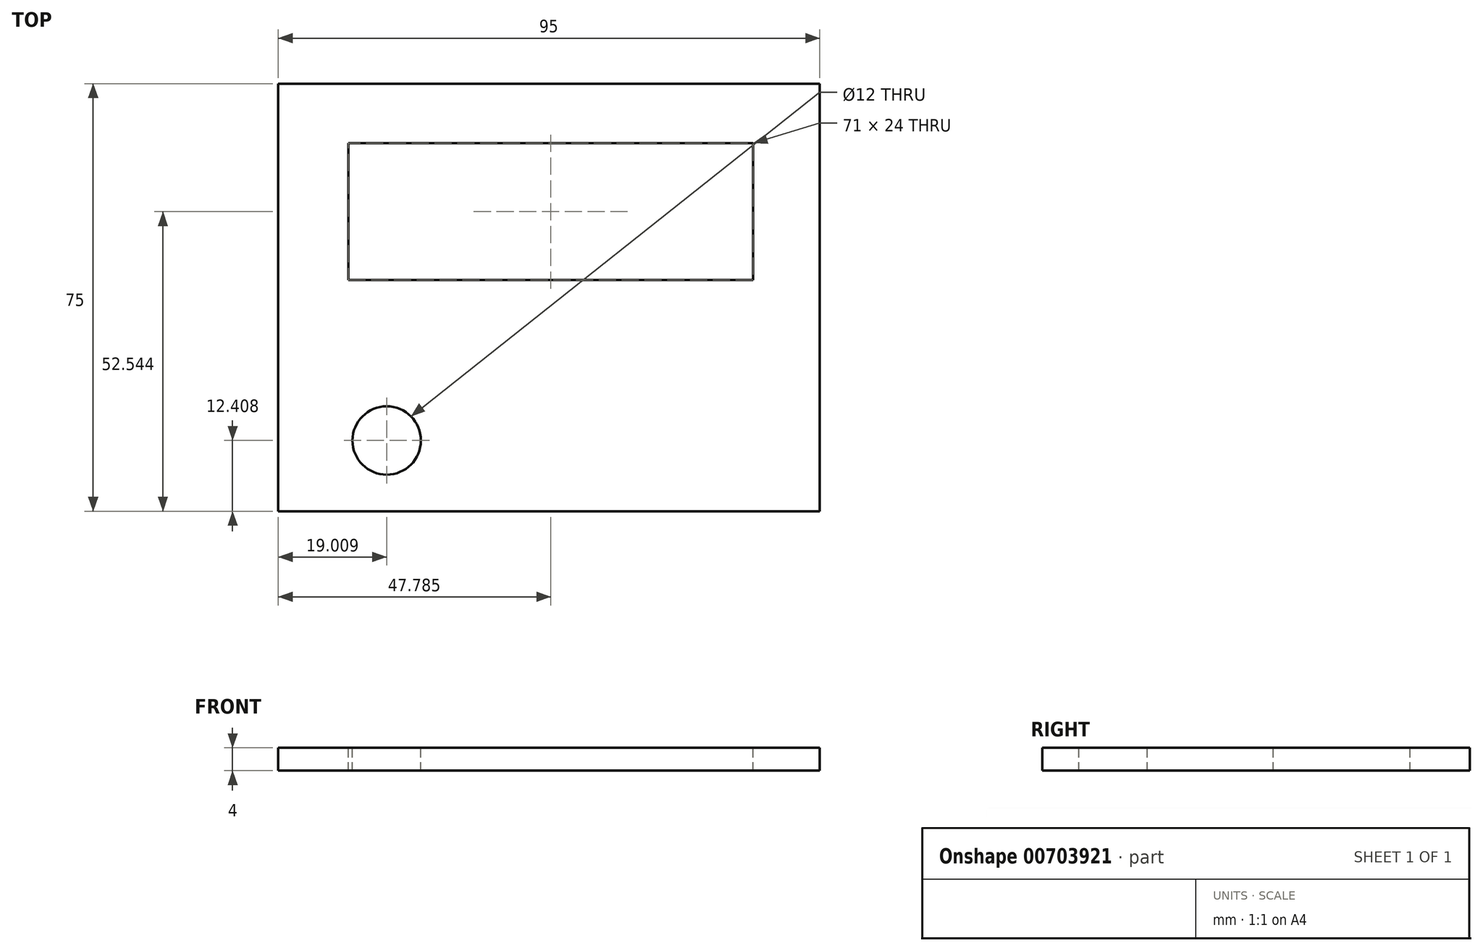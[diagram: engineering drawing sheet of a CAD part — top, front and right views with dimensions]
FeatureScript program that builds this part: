
annotation { "Feature Type Name" : "Feature", "Feature Type Description" : "" }
export const myFeature = defineFeature(function(context is Context, id is Id, definition is map)
    precondition{}
    {
        {
            var Q0;
            Q0=qCreatedBy(makeId("Top.planeOp"),FACE);
            var sketch = newSketch(context, id + "F0", { "sketchPlane" : qUnion([Q0])});
            skLineSegment(sketch, "E0.bottom", {"start": v(-67.71, 35.74) * mm, "end": v(27.29, 35.74) * mm});
            skLineSegment(sketch, "E0.top", {"start": v(-67.71, -39.26) * mm, "end": v(27.29, -39.26) * mm});
            skLineSegment(sketch, "E0.left", {"start": v(-67.71, 35.74) * mm, "end": v(-67.71, -39.26) * mm});
            skLineSegment(sketch, "E0.right", {"start": v(27.29, 35.74) * mm, "end": v(27.29, -39.26) * mm});
            skSolve(sketch);
        }
        {
            var Q0;
            Q0 = qSketchRegion(id + "F0", true);
            extrude(context, id + "F1", {"entities" : qUnion([Q0]), "depth" : 4 * mm, "offsetDistance" : 25 * mm});
        }
        {
            var Q0;
            Q0=makeQuery(id+"F1.opExtrude","CAP_FACE",FACE,{"disambiguationData":[OSD([sQuery(id+"F0.wireOp",EDGE,"E0.bottom"),sQuery(id+"F0.wireOp",EDGE,"E0.top"),sQuery(id+"F0.wireOp",EDGE,"E0.left"),sQuery(id+"F0.wireOp",EDGE,"E0.right")])],"isStart":false});
            var sketch = newSketch(context, id + "F2", { "sketchPlane" : qUnion([Q0])});
            skLineSegment(sketch, "E1.bottom", {"start": v(-55.42, 25.28) * mm, "end": v(15.58, 25.28) * mm});
            skLineSegment(sketch, "E1.top", {"start": v(-55.42, 1.28) * mm, "end": v(15.58, 1.28) * mm});
            skLineSegment(sketch, "E1.left", {"start": v(-55.42, 25.28) * mm, "end": v(-55.42, 1.28) * mm});
            skLineSegment(sketch, "E1.right", {"start": v(15.58, 25.28) * mm, "end": v(15.58, 1.28) * mm});
            skSolve(sketch);
        }
        {
            var Q0;
            Q0 = qSketchRegion(id + "F2", true);
            extrude(context, id + "F3", {"entities" : qUnion([Q0]), "operationType" : NewBodyOperationType.REMOVE, "oppositeDirection" : true, "depth" : 25 * mm, "offsetDistance" : 25 * mm});
        }
        {
            var Q0;
            Q0=makeQuery(id+"F2.imprint","IMPRINT",FACE,{"disambiguationData":[TD([[makeQuery(id+"F2.imprint","IMPRINT",EDGE,{"derivedFrom":sQuery(id+"F2.wireOp",EDGE,"E1.bottom")}),1.0]])]});
            var sketch = newSketch(context, id + "F4", { "sketchPlane" : qUnion([Q0])});
            skLineSegment(sketch, "E2.bottom", {"start": v(-24.31, -5.45) * mm, "end": v(-12.31, -5.45) * mm});
            skLineSegment(sketch, "E2.top", {"start": v(-24.31, -17.45) * mm, "end": v(-12.31, -17.45) * mm});
            skLineSegment(sketch, "E2.left", {"start": v(-24.31, -5.45) * mm, "end": v(-24.31, -17.45) * mm});
            skLineSegment(sketch, "E2.right", {"start": v(-12.31, -5.45) * mm, "end": v(-12.31, -17.45) * mm});
            skSolve(sketch);
        }
        {
            var Q0;
            Q0=makeQuery(id+"F4.imprint","IMPRINT",FACE,{"disambiguationData":[TD([[makeQuery(id+"F4.imprint","IMPRINT",EDGE,{"derivedFrom":sQuery(id+"F4.wireOp",EDGE,"E2.bottom")}),1.0]])]});
            var sketch = newSketch(context, id + "F5", { "sketchPlane" : qUnion([Q0])});
            skCircle(sketch, "E3", {"center": v(-48.7, -26.85) * mm, "radius": 6 * mm});
            skSolve(sketch);
        }
        {
            var Q0;
            Q0 = qSketchRegion(id + "F5", true);
            extrude(context, id + "F6", {"entities" : qUnion([Q0]), "operationType" : NewBodyOperationType.REMOVE, "oppositeDirection" : true, "depth" : 4 * mm, "offsetDistance" : 25 * mm});
        }
    });
